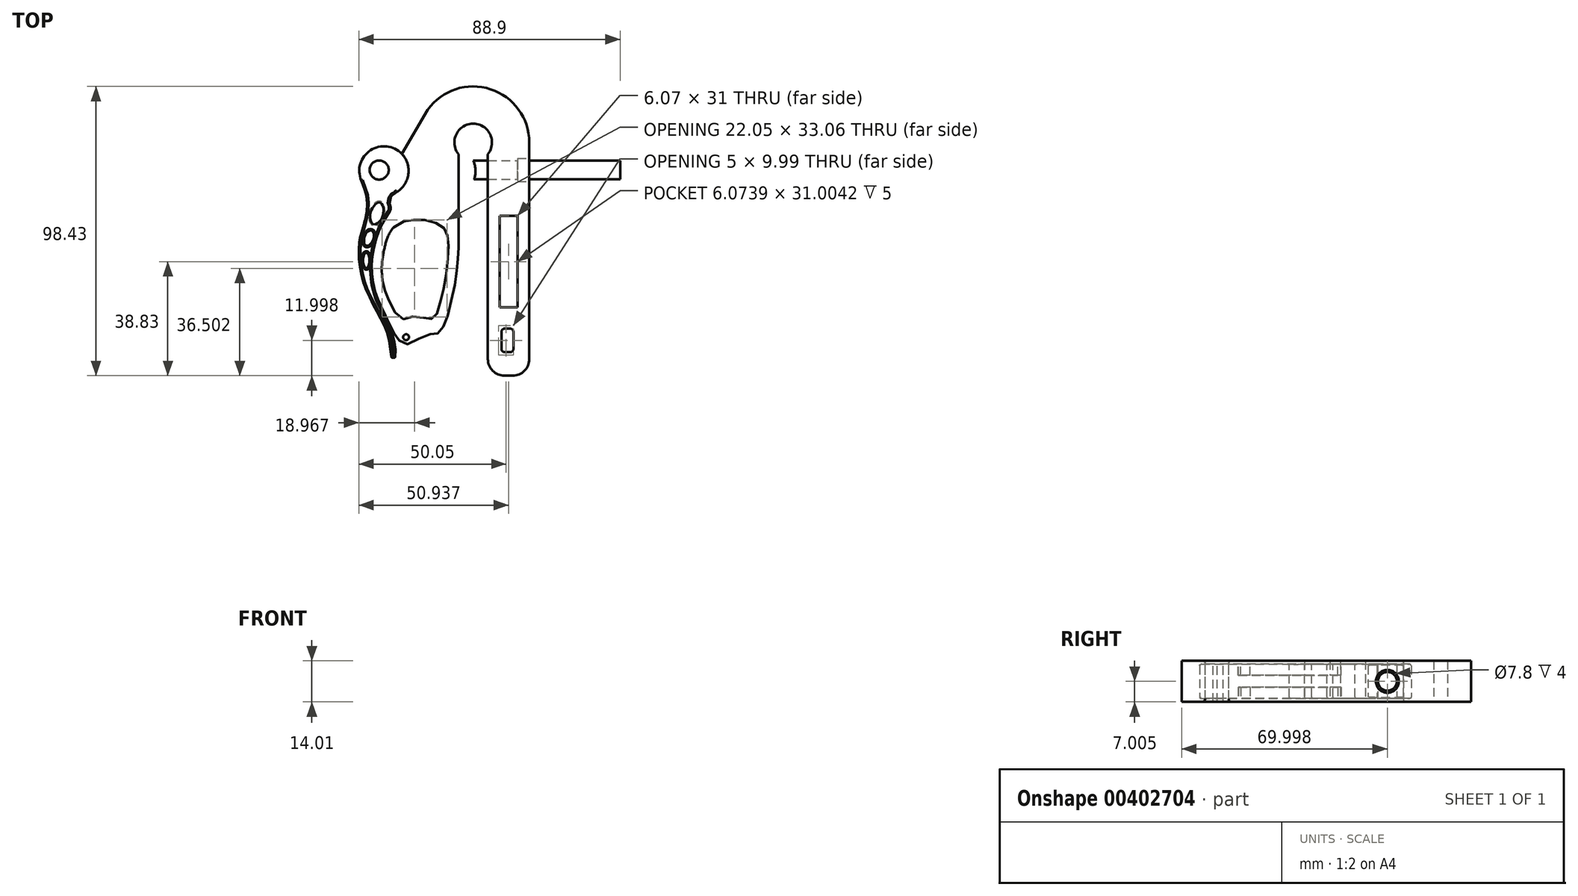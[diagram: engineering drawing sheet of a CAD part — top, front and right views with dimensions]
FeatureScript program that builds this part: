
annotation { "Feature Type Name" : "Feature", "Feature Type Description" : "" }
export const myFeature = defineFeature(function(context is Context, id is Id, definition is map)
    precondition{}
    {
        {
            var Q0;
            Q0=qCreatedBy(makeId("Top.planeOp"),FACE);
            var sketch = newSketch(context, id + "F0", { "sketchPlane" : qUnion([Q0])});
            skLineSegment(sketch, "E0", {"start": v(4.25, 15.7) * mm, "end": v(14.25, 15.7) * mm});
            skSolve(sketch);
        }
        {
            var Q0;
            Q0=qCreatedBy(makeId("Top.planeOp"),FACE);
            var sketch = newSketch(context, id + "F1", { "sketchPlane" : qUnion([Q0])});
            skCircle(sketch, "E1", {"center": v(-9.26, -5.46) * mm, "radius": 3.25 * mm});
            skSolve(sketch);
        }
        {
            var Q0;
            Q0=qCreatedBy(makeId("Top.planeOp"),FACE);
            var sketch = newSketch(context, id + "F2", { "sketchPlane" : qUnion([Q0])});
            skLineSegment(sketch, "E2", {"start": v(-10.3, -5.78) * mm, "end": v(52.53, -5.78) * mm});
            skCircle(sketch, "E3", {"center": v(-7.6, -5.78) * mm, "radius": 8.4 * mm});
            skFitSpline(sketch, "E4", {"points": [v(-15.34, -9.05) * mm, v(-13.72, -13.54) * mm, v(-13.38, -15.5) * mm, v(-13.36, -18.35) * mm, v(-14.1, -22.73) * mm, v(-15.23, -26.6) * mm, v(-15.74, -28.68) * mm, v(-16.08, -31.46) * mm, v(-16.14, -34.4) * mm, v(-15.88, -37.64) * mm, v(-15.5, -39.95) * mm, v(-14.68, -43.49) * mm, v(-13.78, -45.98) * mm, v(-10.97, -51.82) * mm, v(-8.53, -56.37) * mm, v(-7.1, -59.45) * mm, v(-6.08, -62.54) * mm, v(-5.33, -66.95) * mm, v(-5.19, -67.88) * mm, v(-5.05, -69.1) * mm, v(-4.96, -69.3) * mm, v(-4.77, -69.34) * mm, v(-4.09, -69.33) * mm, v(-3.77, -69.02) * mm, v(-3.6, -68.48) * mm, v(-3.65, -67.26) * mm, v(-3.98, -64.6) * mm, v(-4.65, -61.42) * mm, v(-5, -60.18) * mm, v(-5.89, -57.85) * mm, v(-6.72, -56) * mm, v(-8.46, -52.48) * mm, v(-9.55, -50.16) * mm, v(-10.27, -48.37) * mm, v(-10.98, -45.85) * mm, v(-11.43, -43.59) * mm, v(-11.72, -40.7) * mm, v(-11.83, -37.94) * mm, v(-11.8, -36.87) * mm, v(-11.65, -35.17) * mm, v(-11.43, -33.62) * mm, v(-11.1, -32.1) * mm, v(-10.18, -28.54) * mm, v(-9.68, -27) * mm, v(-8.1, -23.55) * mm, v(-6.99, -21.67) * mm, v(-5.8, -19.74) * mm, v(-5.58, -19.3) * mm, v(-5.45, -18.9) * mm, v(-5.4, -18.5) * mm, v(-5.41, -18.12) * mm, v(-5.54, -17.64) * mm, v(-5.72, -17.08) * mm, v(-5.82, -16.42) * mm, v(-5.73, -15.64) * mm, v(-5.6, -15.24) * mm, v(-5.17, -14.43) * mm, v(-4.56, -13.85) * mm, v(-3, -12.81) * mm], "startDerivative": vector(70.6, -181.98) * mm, "endDerivative": vector(100.87, 65.97) * mm});
            skFitSpline(sketch, "E5", {"points": [v(-12.38, -21.6) * mm, v(-12.3, -20.68) * mm, v(-11.9, -19.22) * mm, v(-10.97, -17.7) * mm, v(-10.2, -16.9) * mm, v(-9.44, -16.54) * mm, v(-8.67, -16.63) * mm, v(-8.14, -17.3) * mm, v(-7.79, -18.55) * mm, v(-7.83, -20.2) * mm, v(-8.38, -21.96) * mm, v(-9.3, -23.15) * mm, v(-10.26, -23.86) * mm, v(-10.94, -24) * mm, v(-11.3, -23.86) * mm, v(-11.8, -23.39) * mm, v(-12.2, -22.56) * mm, v(-12.38, -21.6) * mm]});
            skFitSpline(sketch, "E6", {"points": [v(-14.34, -28.7) * mm, v(-14.12, -27.96) * mm, v(-13.63, -27.02) * mm, v(-12.98, -26.32) * mm, v(-12.3, -26.07) * mm, v(-11.62, -26.18) * mm, v(-11.23, -26.62) * mm, v(-11.03, -27.4) * mm, v(-11.15, -28.57) * mm, v(-11.63, -29.94) * mm, v(-12.2, -30.69) * mm, v(-12.9, -31.17) * mm, v(-13.48, -31.26) * mm, v(-13.94, -31.1) * mm, v(-14.28, -30.5) * mm, v(-14.41, -29.7) * mm, v(-14.34, -28.7) * mm]});
            skFitSpline(sketch, "E7", {"points": [v(-14.7, -35.72) * mm, v(-14.54, -34.72) * mm, v(-14.3, -34.12) * mm, v(-13.97, -33.72) * mm, v(-13.5, -33.64) * mm, v(-13.16, -33.88) * mm, v(-12.84, -34.4) * mm, v(-12.6, -35.26) * mm, v(-12.54, -36.12) * mm, v(-12.54, -36.9) * mm, v(-12.72, -37.72) * mm, v(-13.03, -38.4) * mm, v(-13.3, -38.74) * mm, v(-13.7, -38.85) * mm, v(-14.12, -38.56) * mm, v(-14.5, -37.72) * mm, v(-14.68, -36.96) * mm, v(-14.7, -35.72) * mm]});
            skSolve(sketch);
        }
        {
            var Q0;
            {var subQ0=sQuery(id+"F2.wireOp",EDGE,"E4");Q0=makeQuery(id+"F2.imprint","IMPRINT",FACE,{"disambiguationData":[TD([[makeQuery(id+"F2.imprint","IMPRINT",EDGE,{"derivedFrom":subQ0}),1.0]])]});}
            var Q1;
            {var subQ0=sQuery(id+"F2.wireOp",EDGE,"E4");var subQ1=sQuery(id+"F2.wireOp",EDGE,"E3");var subQ2=makeQuery(id+"F2.imprint","INTERSECT",VERTEX,{"disambiguationData":[OD(0.0)],"derivedFrom":[subQ1,subQ0]});Q1=makeQuery(id+"F2.imprint","IMPRINT",FACE,{"disambiguationData":[TD([[makeQuery(id+"F2.imprint","IMPRINT",EDGE,{"disambiguationData":[TD([[subQ2,1.0]])],"derivedFrom":subQ1}),1.0]])]});}
            extrude(context, id + "F3", {"entities" : qUnion([Q0, Q1]), "depth" : 11.64 * mm});
        }
        {
            var Q0;
            Q0=qCreatedBy(makeId("Top.planeOp"),FACE);
            var sketch = newSketch(context, id + "F4", { "sketchPlane" : qUnion([Q0])});
            skCircle(sketch, "E8", {"center": v(-9.26, -5.46) * mm, "radius": 3.25 * mm});
            skSolve(sketch);
        }
        {
            var Q0;
            Q0=makeQuery(id+"F1.imprint","IMPRINT",FACE,{"disambiguationData":[TD([[makeQuery(id+"F1.imprint","IMPRINT",EDGE,{"derivedFrom":sQuery(id+"F1.wireOp",EDGE,"E1")}),1.0]])]});
            extrude(context, id + "F5", {"entities" : qUnion([Q0]), "operationType" : NewBodyOperationType.REMOVE, "endBound" : BoundingType.THROUGH_ALL, "depth" : 25 * mm});
        }
        {
            var Q0;
            Q0=makeQuery(id+"F3.opExtrude","CAP_EDGE",EDGE,{"disambiguationData":[OSD([sQuery(id+"F2.wireOp",EDGE,"E4")])],"isStart":false});
            var Q1;
            Q1=makeQuery(id+"F3.opExtrude","CAP_EDGE",EDGE,{"disambiguationData":[OSD([sQuery(id+"F2.wireOp",EDGE,"E3")])],"isStart":false});
            var Q2;
            Q2=makeQuery(id+"F3.opExtrude","CAP_EDGE",EDGE,{"disambiguationData":[OSD([sQuery(id+"F2.wireOp",EDGE,"E5")])],"isStart":false});
            var Q3;
            Q3=makeQuery(id+"F3.opExtrude","CAP_EDGE",EDGE,{"disambiguationData":[OSD([sQuery(id+"F2.wireOp",EDGE,"E6")])],"isStart":false});
            var Q4;
            Q4=makeQuery(id+"F3.opExtrude","CAP_EDGE",EDGE,{"disambiguationData":[OSD([sQuery(id+"F2.wireOp",EDGE,"E7")])],"isStart":false});
            var Q5;
            Q5=makeQuery(id+"F3.opExtrude","CAP_EDGE",EDGE,{"disambiguationData":[OSD([sQuery(id+"F2.wireOp",EDGE,"E4")])],"isStart":true});
            var Q6;
            Q6=makeQuery(id+"F3.opExtrude","CAP_EDGE",EDGE,{"disambiguationData":[OSD([sQuery(id+"F2.wireOp",EDGE,"E6")])],"isStart":true});
            var Q7;
            Q7=makeQuery(id+"F3.opExtrude","CAP_EDGE",EDGE,{"disambiguationData":[OSD([sQuery(id+"F2.wireOp",EDGE,"E5")])],"isStart":true});
            var Q8;
            Q8=makeQuery(id+"F3.opExtrude","CAP_EDGE",EDGE,{"disambiguationData":[OSD([sQuery(id+"F2.wireOp",EDGE,"E7")])],"isStart":true});
            fillet(context, id + "F6", {"entities" : qUnion([Q0, Q1, Q2, Q3, Q4, Q5, Q6, Q7, Q8]), "radius" : 0.5 * mm, "tangentPropagation" : true, "allowEdgeOverflow" : false});
        }
        {
            var Q0;
            Q0=qCreatedBy(makeId("Top.planeOp"),FACE);
            cPlane(context, id + "F7", {"entities" : qUnion([Q0]), "cplaneType" : CPlaneType.OFFSET, "offset" : 5.83 * mm, "width" : 150 * mm, "height" : 150 * mm});
        }
        {
            var Q0;
            Q0=qCreatedBy(id+"F7.planeOp",FACE);
            var sketch = newSketch(context, id + "F8", { "sketchPlane" : qUnion([Q0])});
            skLineSegment(sketch, "E9", {"start": v(0.79, -5.46) * mm, "end": v(40, -5.46) * mm});
            skLineSegment(sketch, "E10", {"start": v(-9.26, -5.46) * mm, "end": v(10.7, -5.46) * mm, "construction": true});
            skSolve(sketch);
        }
        {
            var Q0;
            Q0=qCreatedBy(makeId("Right.planeOp"),FACE);
            cPlane(context, id + "F9", {"entities" : qUnion([Q0]), "cplaneType" : CPlaneType.OFFSET, "offset" : 50 * mm, "width" : 150 * mm, "height" : 150 * mm});
        }
        {
            var Q0;
            Q0=qCreatedBy(id+"F9.planeOp",FACE);
            var sketch = newSketch(context, id + "F10", { "sketchPlane" : qUnion([Q0])});
            skCircle(sketch, "E11", {"center": v(-5.46, 5.83) * mm, "radius": 3.2 * mm});
            skSolve(sketch);
        }
        {
            var Q0;
            Q0 = qSketchRegion(id + "F10", true);
            extrude(context, id + "F11", {"entities" : qUnion([Q0]), "endBound" : BoundingType.UP_TO_NEXT, "oppositeDirection" : true, "depth" : 25 * mm});
        }
        {
            var Q0;
            Q0=makeQuery(id+"F3.opExtrude","SWEPT_BODY",BODY,{"disambiguationData":[OSD([sQuery(id+"F2.wireOp",EDGE,"E3"),sQuery(id+"F2.wireOp",EDGE,"E4"),sQuery(id+"F2.wireOp",EDGE,"E5"),sQuery(id+"F2.wireOp",EDGE,"E6"),sQuery(id+"F2.wireOp",EDGE,"E7")])]});
            var Q1;
            Q1=qCreatedBy(makeId("Right.planeOp"),FACE);
            transform(context, id + "F12", {"entities" : qUnion([Q0]), "transformType" : TransformType.TRANSLATION_DISTANCE, "transformDirection" : qUnion([Q1]), "distance" : 22.75 * mm, "oppositeDirection" : true, "makeCopy" : false});
        }
        {
            var Q0;
            Q0=qCreatedBy(id+"F7.planeOp",FACE);
            var sketch = newSketch(context, id + "F13", { "sketchPlane" : qUnion([Q0])});
            skCircle(sketch, "E12", {"center": v(0, 3.9) * mm, "radius": 6.4 * mm, "construction": true});
            skArc(sketch, "E13", {"start": v(-19.07, 3.9) * mm, "mid": v(0, 22.97) * mm, "end": v(19.07, 3.9) * mm, "construction": true});
            skLineSegment(sketch, "E14", {"start": v(-5, -0.1) * mm, "end": v(-5, -75.46) * mm, "construction": true});
            skLineSegment(sketch, "E15.MirrorCS", {"start": v(5, -0.1) * mm, "end": v(5, -75.46) * mm, "construction": true});
            skLineSegment(sketch, "E16", {"start": v(19.07, 3.9) * mm, "end": v(19.07, -75.46) * mm, "construction": true});
            skFitSpline(sketch, "E17", {"points": [v(-29.55, -55.64) * mm, v(-25.18, -64.13) * mm, v(-21.63, -66.58) * mm, v(-16.63, -66.05) * mm, v(-13.4, -64.72) * mm, v(-4.95, -27.88) * mm], "startDerivative": vector(31.63, -62.74) * mm, "endDerivative": vector(-2.46, 128.25) * mm, "construction": true});
            skLineSegment(sketch, "E18", {"start": v(5, -75.46) * mm, "end": v(19.07, -75.46) * mm, "construction": true});
            skFitSpline(sketch, "E19", {"points": [v(-30.52, -33.64) * mm, v(-27.1, -25.02) * mm], "startDerivative": vector(2.2, 9.83) * mm, "endDerivative": vector(6.97, 8.55) * mm});
            skFitSpline(sketch, "E20", {"points": [v(-29.56, -21.5) * mm, v(-31.44, -24.87) * mm, v(-32.7, -27.93) * mm, v(-33.75, -31.93) * mm], "startDerivative": vector(-6, -10.28) * mm, "endDerivative": vector(-2.89, -11.93) * mm});
            skArc(sketch, "E21", {"start": v(-15.47, 15.06) * mm, "mid": v(5.86, 22.05) * mm, "end": v(19.07, 3.9) * mm});
            skLineSegment(sketch, "E22", {"start": v(19.07, -75.46) * mm, "end": v(19.07, 3.9) * mm});
            skLineSegment(sketch, "E23", {"start": v(19.07, -75.46) * mm, "end": v(5, -75.46) * mm});
            skLineSegment(sketch, "E24", {"start": v(5, -0.1) * mm, "end": v(5, -75.46) * mm});
            skArc(sketch, "E25", {"start": v(5, -0.1) * mm, "mid": v(0, 10.3) * mm, "end": v(-5, -0.1) * mm});
            skLineSegment(sketch, "E26", {"start": v(-4.95, -27.9) * mm, "end": v(-5, -0.1) * mm});
            skFitSpline(sketch, "E27", {"points": [v(-25.67, -12.76) * mm, v(-27.72, -14.22) * mm, v(-28.4, -15.5) * mm, v(-28.51, -16.73) * mm, v(-28.14, -18) * mm, v(-28.13, -18.84) * mm, v(-28.41, -19.6) * mm, v(-29.02, -20.64) * mm, v(-29.56, -21.5) * mm, v(-30.98, -24) * mm, v(-32.51, -27.39) * mm, v(-33.41, -30.54) * mm, v(-33.75, -31.93) * mm, v(-34.24, -34.36) * mm, v(-34.51, -37.32) * mm, v(-34.46, -39.9) * mm, v(-34.23, -42.75) * mm, v(-33.75, -45.53) * mm, v(-33.01, -48.2) * mm, v(-31.95, -50.62) * mm, v(-30.74, -53.2) * mm, v(-29.6, -55.6) * mm, v(-28.26, -58.51) * mm, v(-26.18, -62.25) * mm, v(-24.97, -63.68) * mm, v(-21.84, -64.66) * mm, v(-16.6, -61.83) * mm, v(-13.01, -61.27) * mm, v(-11.67, -60.82) * mm, v(-9.77, -58.07) * mm, v(-8, -52.34) * mm, v(-6.06, -43.28) * mm, v(-5.29, -37.11) * mm, v(-5, -32.73) * mm, v(-4.95, -27.9) * mm], "startDerivative": vector(-135.22, -94.54) * mm, "endDerivative": vector(1.05, 140.54) * mm});
            skFitSpline(sketch, "E28", {"points": [v(-30.52, -33.64) * mm, v(-31.05, -36.67) * mm, v(-31.2, -39.39) * mm, v(-30.86, -43.33) * mm, v(-29.86, -47.04) * mm, v(-28.05, -51.13) * mm, v(-24.43, -56.12) * mm, v(-21.45, -55.55) * mm, v(-17.16, -55.66) * mm, v(-14.75, -56.15) * mm, v(-13.06, -55.7) * mm, v(-11.12, -50.32) * mm, v(-9.79, -44.62) * mm, v(-8.6, -35.77) * mm, v(-8.41, -30.11) * mm, v(-9.03, -26.64) * mm, v(-10.4, -24.74) * mm, v(-14.21, -22.93) * mm, v(-19.02, -22.36) * mm, v(-22.87, -22.79) * mm, v(-27.1, -25.02) * mm], "startDerivative": vector(-14.95, -76.87) * mm, "endDerivative": vector(-98.96, -93.3) * mm});
            skLineSegment(sketch, "E29", {"start": v(-24.26, 0) * mm, "end": v(-15.47, 15.06) * mm});
            skLineSegment(sketch, "E30", {"start": v(-28.18, -63.7) * mm, "end": v(-3.5, -59.7) * mm, "construction": true});
            skPoint(sketch, "E31", {"position": v(-23.56, -66.91) * mm});
            skLineSegment(sketch, "E32", {"start": v(-9.26, -5.46) * mm, "end": v(-36.37, -5.46) * mm, "construction": true});
            skArc(sketch, "E33", {"start": v(-24.26, 0) * mm, "mid": v(-22.07, -6.9) * mm, "end": v(-25.99, -12.98) * mm});
            skSolve(sketch);
        }
        {
            var Q0;
            Q0=makeQuery(id+"F13.imprint","IMPRINT",FACE,{"disambiguationData":[TD([[makeQuery(id+"F13.imprint","IMPRINT",EDGE,{"derivedFrom":sQuery(id+"F13.wireOp",EDGE,"E19")}),1.0]])]});
            extrude(context, id + "F14", {"entities" : qUnion([Q0]), "endBound" : BoundingType.SYMMETRIC, "depth" : 14 * mm});
        }
        {
            var Q0;
            Q0=makeQuery(id+"F3.opExtrude","SWEPT_BODY",BODY,{"disambiguationData":[OSD([sQuery(id+"F2.wireOp",EDGE,"E3"),sQuery(id+"F2.wireOp",EDGE,"E4"),sQuery(id+"F2.wireOp",EDGE,"E5"),sQuery(id+"F2.wireOp",EDGE,"E6"),sQuery(id+"F2.wireOp",EDGE,"E7")])]});
            var Q1;
            Q1=makeQuery(id+"F14.opExtrude","SWEPT_BODY",BODY,{"disambiguationData":[OSD([sQuery(id+"F13.wireOp",EDGE,"E20"),sQuery(id+"F13.wireOp",EDGE,"V2Bz2KIU-wCmZ-UWWS-2qdv-DvyFVtP3OgTG"),sQuery(id+"F13.wireOp",EDGE,"E21"),sQuery(id+"F13.wireOp",EDGE,"E22"),sQuery(id+"F13.wireOp",EDGE,"E23"),sQuery(id+"F13.wireOp",EDGE,"E24"),sQuery(id+"F13.wireOp",EDGE,"E25"),sQuery(id+"F13.wireOp",EDGE,"E26"),sQuery(id+"F13.wireOp",EDGE,"RwT07Lts-7mHV-BUIf-HWwy-4UaDgbhcZAHS"),sQuery(id+"F13.wireOp",EDGE,"E27")])]});
            booleanBodies(context, id + "F15", {"operationType" : BooleanOperationType.SUBTRACTION, "tools" : qUnion([Q0]), "targets" : qUnion([Q1]), "keepTools" : true});
        }
        {
            var Q0;
            Q0=makeQuery(id+"F14.opExtrude","CAP_FACE",FACE,{"disambiguationData":[OSD([sQuery(id+"F13.wireOp",EDGE,"E20"),sQuery(id+"F13.wireOp",EDGE,"V2Bz2KIU-wCmZ-UWWS-2qdv-DvyFVtP3OgTG"),sQuery(id+"F13.wireOp",EDGE,"E21"),sQuery(id+"F13.wireOp",EDGE,"E22"),sQuery(id+"F13.wireOp",EDGE,"E23"),sQuery(id+"F13.wireOp",EDGE,"E24"),sQuery(id+"F13.wireOp",EDGE,"E25"),sQuery(id+"F13.wireOp",EDGE,"E26"),sQuery(id+"F13.wireOp",EDGE,"RwT07Lts-7mHV-BUIf-HWwy-4UaDgbhcZAHS"),sQuery(id+"F13.wireOp",EDGE,"E27")])],"isStart":false});
            var sketch = newSketch(context, id + "F16", { "sketchPlane" : qUnion([Q0])});
            skLineSegment(sketch, "E34.0", {"start": v(9, -21.13) * mm, "end": v(9, -52.13) * mm});
            skLineSegment(sketch, "E35.0", {"start": v(15.07, -52.13) * mm, "end": v(15.07, -21.13) * mm});
            skLineSegment(sketch, "E36", {"start": v(9, -21.13) * mm, "end": v(15.07, -21.13) * mm});
            skLineSegment(sketch, "E37", {"start": v(9, -52.13) * mm, "end": v(15.07, -52.13) * mm});
            skSolve(sketch);
        }
        {
            var Q0;
            Q0=makeQuery(id+"F16.imprint","IMPRINT",FACE,{"disambiguationData":[TD([[makeQuery(id+"F16.imprint","IMPRINT",EDGE,{"derivedFrom":sQuery(id+"F16.wireOp",EDGE,"E34.0")}),1.0]])]});
            extrude(context, id + "F17", {"entities" : qUnion([Q0]), "operationType" : NewBodyOperationType.REMOVE, "oppositeDirection" : true, "depth" : 5 * mm});
        }
        {
            var Q0;
            Q0=makeQuery(id+"F14.opExtrude","CAP_FACE",FACE,{"disambiguationData":[OSD([sQuery(id+"F13.wireOp",EDGE,"E20"),sQuery(id+"F13.wireOp",EDGE,"V2Bz2KIU-wCmZ-UWWS-2qdv-DvyFVtP3OgTG"),sQuery(id+"F13.wireOp",EDGE,"E21"),sQuery(id+"F13.wireOp",EDGE,"E22"),sQuery(id+"F13.wireOp",EDGE,"E23"),sQuery(id+"F13.wireOp",EDGE,"E24"),sQuery(id+"F13.wireOp",EDGE,"E25"),sQuery(id+"F13.wireOp",EDGE,"E26"),sQuery(id+"F13.wireOp",EDGE,"RwT07Lts-7mHV-BUIf-HWwy-4UaDgbhcZAHS"),sQuery(id+"F13.wireOp",EDGE,"E27")])],"isStart":true});
            var sketch = newSketch(context, id + "F18", { "sketchPlane" : qUnion([Q0])});
            skLineSegment(sketch, "E38.0", {"start": v(9, 21.13) * mm, "end": v(9, 52.13) * mm});
            skLineSegment(sketch, "E39.0", {"start": v(15.07, 52.13) * mm, "end": v(15.07, 21.13) * mm});
            skLineSegment(sketch, "E40", {"start": v(9, 52.13) * mm, "end": v(15.07, 52.13) * mm});
            skLineSegment(sketch, "E41", {"start": v(9, 21.13) * mm, "end": v(15.07, 21.13) * mm});
            skSolve(sketch);
        }
        {
            var Q0;
            Q0=makeQuery(id+"F18.imprint","IMPRINT",FACE,{"disambiguationData":[TD([[makeQuery(id+"F18.imprint","IMPRINT",EDGE,{"derivedFrom":sQuery(id+"F18.wireOp",EDGE,"E38.0")}),-1.0]])]});
            extrude(context, id + "F19", {"entities" : qUnion([Q0]), "operationType" : NewBodyOperationType.REMOVE, "oppositeDirection" : true, "depth" : 5 * mm});
        }
        {
            var Q0;
            Q0=makeQuery(id+"F14.opExtrude","SWEPT_FACE",FACE,{"disambiguationData":[OSD([sQuery(id+"F13.wireOp",EDGE,"E22")])]});
            var sketch = newSketch(context, id + "F20", { "sketchPlane" : qUnion([Q0])});
            skCircle(sketch, "E42", {"center": v(-5.46, 5.83) * mm, "radius": 3.9 * mm});
            skSolve(sketch);
        }
        {
            var Q0;
            Q0 = qSketchRegion(id + "F20", true);
            extrude(context, id + "F21", {"entities" : qUnion([Q0]), "operationType" : NewBodyOperationType.REMOVE, "oppositeDirection" : true, "depth" : 4 * mm});
        }
        {
            var Q0;
            Q0=makeQuery(id+"F16.imprint","IMPRINT",FACE,{"disambiguationData":[TD([[makeQuery(id+"F16.imprint","IMPRINT",EDGE,{"derivedFrom":sQuery(id+"F16.wireOp",EDGE,"E34.0")}),-1.0]])]});
            var sketch = newSketch(context, id + "F22", { "sketchPlane" : qUnion([Q0])});
            skLineSegment(sketch, "E43.bottom", {"start": v(9.65, -59.46) * mm, "end": v(13.65, -59.46) * mm});
            skLineSegment(sketch, "E43.top", {"start": v(9.65, -67.46) * mm, "end": v(13.65, -67.46) * mm});
            skLineSegment(sketch, "E43.left", {"start": v(9.65, -59.46) * mm, "end": v(9.65, -67.46) * mm});
            skLineSegment(sketch, "E43.right", {"start": v(13.65, -59.46) * mm, "end": v(13.65, -67.46) * mm});
            skPoint(sketch, "E43.middle", {"position": v(11.65, -63.46) * mm});
            skSolve(sketch);
        }
        {
            var Q0;
            Q0 = qSketchRegion(id + "F22", true);
            extrude(context, id + "F23", {"entities" : qUnion([Q0]), "operationType" : NewBodyOperationType.REMOVE, "endBound" : BoundingType.THROUGH_ALL, "oppositeDirection" : true, "depth" : 25 * mm});
        }
        {
            var Q0;
            Q0=makeQuery(id+"F23.boolean.opBoolean","COPY",EDGE,{"derivedFrom":makeQuery(id+"F23.opExtrude","SWEPT_EDGE",EDGE,{"disambiguationData":[OSD([sQuery(id+"F22.wireOp",EDGE,"E43.bottom"),sQuery(id+"F22.wireOp",EDGE,"E43.right")])]})});
            var Q1;
            Q1=makeQuery(id+"F23.boolean.opBoolean","COPY",EDGE,{"derivedFrom":makeQuery(id+"F23.opExtrude","SWEPT_EDGE",EDGE,{"disambiguationData":[OSD([sQuery(id+"F22.wireOp",EDGE,"E43.top"),sQuery(id+"F22.wireOp",EDGE,"E43.right")])]})});
            var Q2;
            Q2=makeQuery(id+"F23.boolean.opBoolean","COPY",FACE,{"derivedFrom":makeQuery(id+"F23.opExtrude","SWEPT_FACE",FACE,{"disambiguationData":[OSD([sQuery(id+"F22.wireOp",EDGE,"E43.left")])]})});
            fillet(context, id + "F24", {"entities" : qUnion([Q0, Q1, Q2]), "radius" : 1 * mm, "tangentPropagation" : true, "allowEdgeOverflow" : false});
        }
        {
            var Q0;
            Q0=makeQuery(id+"F14.opExtrude","SWEPT_EDGE",EDGE,{"disambiguationData":[OSD([sQuery(id+"F13.wireOp",EDGE,"E23"),sQuery(id+"F13.wireOp",EDGE,"E24")])]});
            var Q1;
            Q1=makeQuery(id+"F14.opExtrude","SWEPT_EDGE",EDGE,{"disambiguationData":[OSD([sQuery(id+"F13.wireOp",EDGE,"E22"),sQuery(id+"F13.wireOp",EDGE,"E23")])]});
            fillet(context, id + "F25", {"entities" : qUnion([Q0, Q1]), "radius" : 5.65 * mm, "tangentPropagation" : true, "allowEdgeOverflow" : false});
        }
        {
            var Q0;
            Q0=makeQuery(id+"F13.imprint","IMPRINT",FACE,{"disambiguationData":[TD([[makeQuery(id+"F13.imprint","IMPRINT",EDGE,{"derivedFrom":sQuery(id+"F13.wireOp",EDGE,"E19")}),-1.0]])]});
            extrude(context, id + "F26", {"entities" : qUnion([Q0]), "operationType" : NewBodyOperationType.ADD, "endBound" : BoundingType.SYMMETRIC, "depth" : 4 * mm});
        }
        {
            var Q0;
            Q0=qCreatedBy(id+"F7.planeOp",FACE);
            var sketch = newSketch(context, id + "F27", { "sketchPlane" : qUnion([Q0])});
            skCircle(sketch, "E44", {"center": v(-22.83, -62.36) * mm, "radius": 9 * mm});
            skSolve(sketch);
        }
        {
            var Q0;
            Q0=makeQuery(id+"F16.imprint","IMPRINT",FACE,{"disambiguationData":[TD([[makeQuery(id+"F16.imprint","IMPRINT",EDGE,{"derivedFrom":sQuery(id+"F16.wireOp",EDGE,"E34.0")}),-1.0]])]});
            var sketch = newSketch(context, id + "F28", { "sketchPlane" : qUnion([Q0])});
            skCircle(sketch, "E45", {"center": v(-22.83, -62.36) * mm, "radius": 1 * mm});
            skSolve(sketch);
        }
        {
            var Q0;
            Q0=makeQuery(id+"F16.imprint","IMPRINT",FACE,{"disambiguationData":[TD([[makeQuery(id+"F16.imprint","IMPRINT",EDGE,{"derivedFrom":sQuery(id+"F16.wireOp",EDGE,"E34.0")}),-1.0]])]});
            var sketch = newSketch(context, id + "F29", { "sketchPlane" : qUnion([Q0])});
            skLineSegment(sketch, "E46", {"start": v(-8.46, -61.21) * mm, "end": v(-23.93, -62.07) * mm});
            skFitSpline(sketch, "E47", {"points": [v(-23.93, -62.07) * mm, v(-25.64, -61.49) * mm, v(-27.23, -59.23) * mm, v(-30.33, -53.01) * mm, v(-32.59, -48.44) * mm, v(-33.93, -44.48) * mm], "startDerivative": vector(-13.51, 2.64) * mm, "endDerivative": vector(-5.83, 19.4) * mm});
            skLineSegment(sketch, "E48", {"start": v(-33.93, -44.48) * mm, "end": v(-38.95, -44.48) * mm});
            skLineSegment(sketch, "E49", {"start": v(-38.95, -44.48) * mm, "end": v(-39.44, -69.94) * mm});
            skLineSegment(sketch, "E50", {"start": v(-39.44, -69.94) * mm, "end": v(-8.46, -70.25) * mm});
            skLineSegment(sketch, "E51", {"start": v(-8.46, -70.25) * mm, "end": v(-8.46, -61.21) * mm});
            skSolve(sketch);
        }
        {
            var Q0;
            {var subQ6=sQuery(id+"F29.wireOp",EDGE,"E49");Q0=makeQuery(id+"F29.imprint","IMPRINT",FACE,{"disambiguationData":[TD([[makeQuery(id+"F29.imprint","IMPRINT",EDGE,{"derivedFrom":subQ6}),1.0]])]});}
            extrude(context, id + "F30", {"entities" : qUnion([Q0]), "endBound" : BoundingType.SYMMETRIC, "depth" : 25 * mm});
        }
        {
            var Q0;
            Q0=makeQuery(id+"F30.opExtrude","SWEPT_BODY",BODY,{"disambiguationData":[OSD([sQuery(id+"F13.wireOp",EDGE,"E27"),sQuery(id+"F29.wireOp",EDGE,"E46"),sQuery(id+"F29.wireOp",EDGE,"E48"),sQuery(id+"F29.wireOp",EDGE,"E49"),sQuery(id+"F29.wireOp",EDGE,"E50"),sQuery(id+"F29.wireOp",EDGE,"E51")])]});
            var Q1;
            Q1=makeQuery(id+"F14.opExtrude","SWEPT_BODY",BODY,{"disambiguationData":[OSD([sQuery(id+"F13.wireOp",EDGE,"E19"),sQuery(id+"F13.wireOp",EDGE,"E20"),sQuery(id+"F13.wireOp",EDGE,"E21"),sQuery(id+"F13.wireOp",EDGE,"E22"),sQuery(id+"F13.wireOp",EDGE,"E23"),sQuery(id+"F13.wireOp",EDGE,"E24"),sQuery(id+"F13.wireOp",EDGE,"E25"),sQuery(id+"F13.wireOp",EDGE,"E26"),sQuery(id+"F13.wireOp",EDGE,"RwT07Lts-7mHV-BUIf-HWwy-4UaDgbhcZAHS"),sQuery(id+"F13.wireOp",EDGE,"E27"),sQuery(id+"F13.wireOp",EDGE,"E28"),sQuery(id+"F13.wireOp",EDGE,"E29")])]});
            booleanBodies(context, id + "F31", {"operationType" : BooleanOperationType.SUBTRACTION, "tools" : qUnion([Q0]), "targets" : qUnion([Q1])});
        }
        {
            var Q0;
            Q0 = qSketchRegion(id + "F28", true);
            extrude(context, id + "F32", {"entities" : qUnion([Q0]), "operationType" : NewBodyOperationType.REMOVE, "endBound" : BoundingType.THROUGH_ALL, "oppositeDirection" : true, "depth" : 25 * mm});
        }
    });
